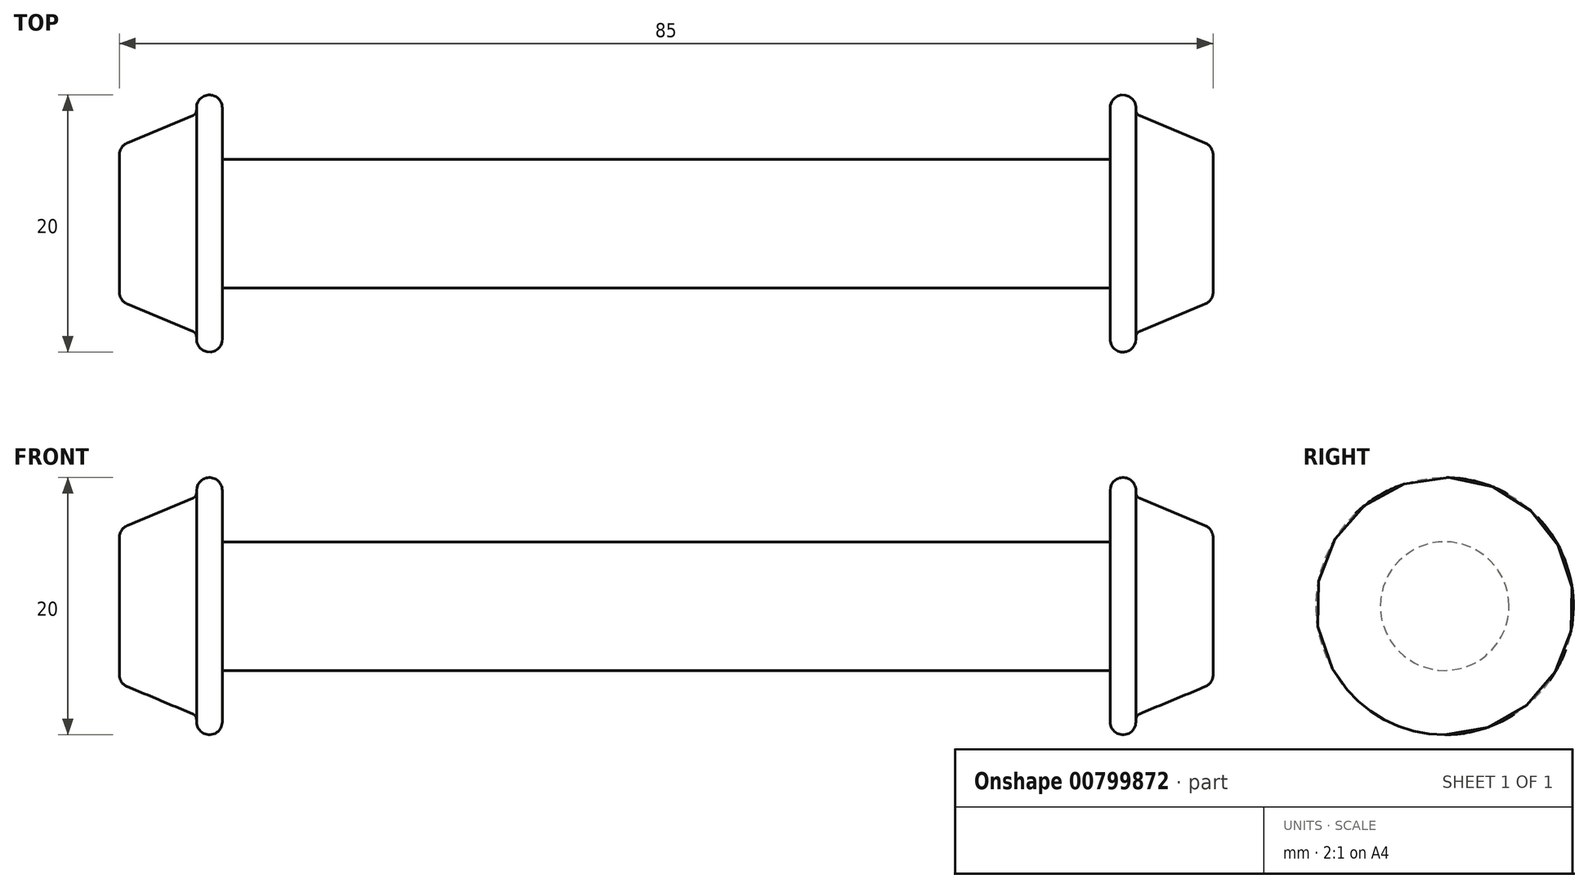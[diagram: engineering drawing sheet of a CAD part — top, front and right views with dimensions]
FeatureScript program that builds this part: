
annotation { "Feature Type Name" : "Feature", "Feature Type Description" : "" }
export const myFeature = defineFeature(function(context is Context, id is Id, definition is map)
    precondition{}
    {
        {
            var Q0;
            Q0=qCreatedBy(makeId("Front.planeOp"),FACE);
            var sketch = newSketch(context, id + "F0", { "sketchPlane" : qUnion([Q0])});
            skLineSegment(sketch, "E0", {"start": v(-34.5, -383.12) * mm, "end": v(0, -383.12) * mm});
            skLineSegment(sketch, "E1", {"start": v(-41.88, -381.87) * mm, "end": v(-36.8, -379.75) * mm});
            skLineSegment(sketch, "E2", {"start": v(-34.5, -379.12) * mm, "end": v(-34.5, -388.12) * mm});
            skArc(sketch, "E3", {"start": v(-34.5, -379.12) * mm, "mid": v(-35.5, -378.12) * mm, "end": v(-36.5, -379.12) * mm});
            skLineSegment(sketch, "E4", {"start": v(-42.5, -382.79) * mm, "end": v(-42.5, -388.12) * mm});
            skArc(sketch, "E5", {"start": v(-41.88, -381.87) * mm, "mid": v(-42.33, -382.23) * mm, "end": v(-42.5, -382.79) * mm});
            skLineSegment(sketch, "E6", {"start": v(-36.5, -379.12) * mm, "end": v(-36.5, -379.29) * mm});
            skArc(sketch, "E7", {"start": v(-36.8, -379.75) * mm, "mid": v(-36.58, -379.57) * mm, "end": v(-36.5, -379.29) * mm});
            skLineSegment(sketch, "E8.trimOffspring", {"start": v(-36.5, -379.29) * mm, "end": v(-36.5, -379.12) * mm});
            skLineSegment(sketch, "E9", {"start": v(0, -388.12) * mm, "end": v(0, -383.12) * mm});
            skLineSegment(sketch, "E10.trimOffspring", {"start": v(0, -388.12) * mm, "end": v(-42.5, -388.12) * mm});
            skSolve(sketch);
        }
        {
            var Q0;
            Q0 = qSketchRegion(id + "F0", true);
            var Q1;
            Q1=sQuery(id+"F0.wireOp",EDGE,"E10.trimOffspring");
            revolve(context, id + "F1", {"surfaceOperationType" : NewSurfaceOperationType.NEW, "entities" : qUnion([Q0]), "axis" : qUnion([Q1]), "revolveType" : RevolveType.FULL});
        }
        {
            var Q0;
            Q0=makeQuery(id+"F1.opRevolve","SWEPT_BODY",BODY,{"disambiguationData":[OSD([sQuery(id+"F0.wireOp",EDGE,"E0"),sQuery(id+"F0.wireOp",EDGE,"E1"),sQuery(id+"F0.wireOp",EDGE,"E2"),sQuery(id+"F0.wireOp",EDGE,"E3"),sQuery(id+"F0.wireOp",EDGE,"E4"),sQuery(id+"F0.wireOp",EDGE,"E5"),sQuery(id+"F0.wireOp",EDGE,"E7"),sQuery(id+"F0.wireOp",EDGE,"E8.trimOffspring"),sQuery(id+"F0.wireOp",EDGE,"E9"),sQuery(id+"F0.wireOp",EDGE,"E10.trimOffspring")])]});
            var Q1;
            Q1=makeQuery(id+"F1.opRevolve","SWEPT_FACE",FACE,{"disambiguationData":[OSD([sQuery(id+"F0.wireOp",EDGE,"E9")])]});
            mirror(context, id + "F2", {"operationType" : NewBodyOperationType.ADD, "entities" : qUnion([Q0]), "mirrorPlane" : qUnion([Q1])});
        }
    });
